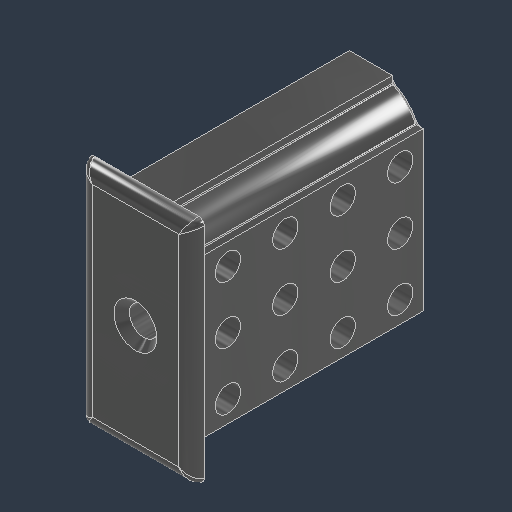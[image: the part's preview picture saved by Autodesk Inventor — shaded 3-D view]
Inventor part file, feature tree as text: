
AUTODESK INVENTOR PART (.ipt)
format: ipt  version: 2024.3 (Build 283343000, 343)  size: 299,520 bytes
history: native  units: in
note: dims shown in document units (in); Inventor stores cm internally (conversion verified against a paired STEP export)
features: sketch x4, extrude x2, fillet x2, hole x2, chamfer x1, pattern_linear x1
ambient origin geometry x8: Origin, YZ Plane, XZ Plane, XY Plane, X Axis, Y Axis, Z Axis, Center Point
bodies: Solid1 (feature_tree)
feature tree (12):
  extrude  "Extrusion1"  Depth=2.0in TaperAngle=0.0deg
  extrude  "Extrusion2"  Depth=2.0in
  fillet  "Fillet1"  Radius=0.1in
  fillet  "Fillet2"  Radius=0.125in
  hole  "Hole1"  [1 undecoded]
  hole  "Hole2"  [1 undecoded]
  chamfer  "Chamfer1"  Distance=1.0in
  pattern_linear  "Rectangular Pattern1"  Count1=4 Spacing1=0.5in
  sketch  "Sketch1"  dims[d0=0.005in d1=2.0in d2=0.0in]
  sketch  "Sketch2"  dims[d3=1.0in d4=2.0in d5=0.1in d6=0.0in d7=0.125in]
  sketch  "Sketch3"  dims[d8=0.05in]
  sketch  "Sketch4"  dims[d9=0.25in d10=0.75in d11=0.375in d12=0.25in d13=0.5635in d14=1.0in d15=0.8108in d16=0.221in d17=0.75in d18=0.385in d19=0.25in d20=0.5635in d21=1.0in d22=0.8108in d23=0.05in d24=0.125in d25=45.0deg d26=0.25in d27=1.0in d28=1.5748in d30=0.5in]
note: 2 required parameter values undecoded (feature->parameter linkage not recoverable at this tier; creation-order binding heuristic only, values carry confidence <= 0.55)
